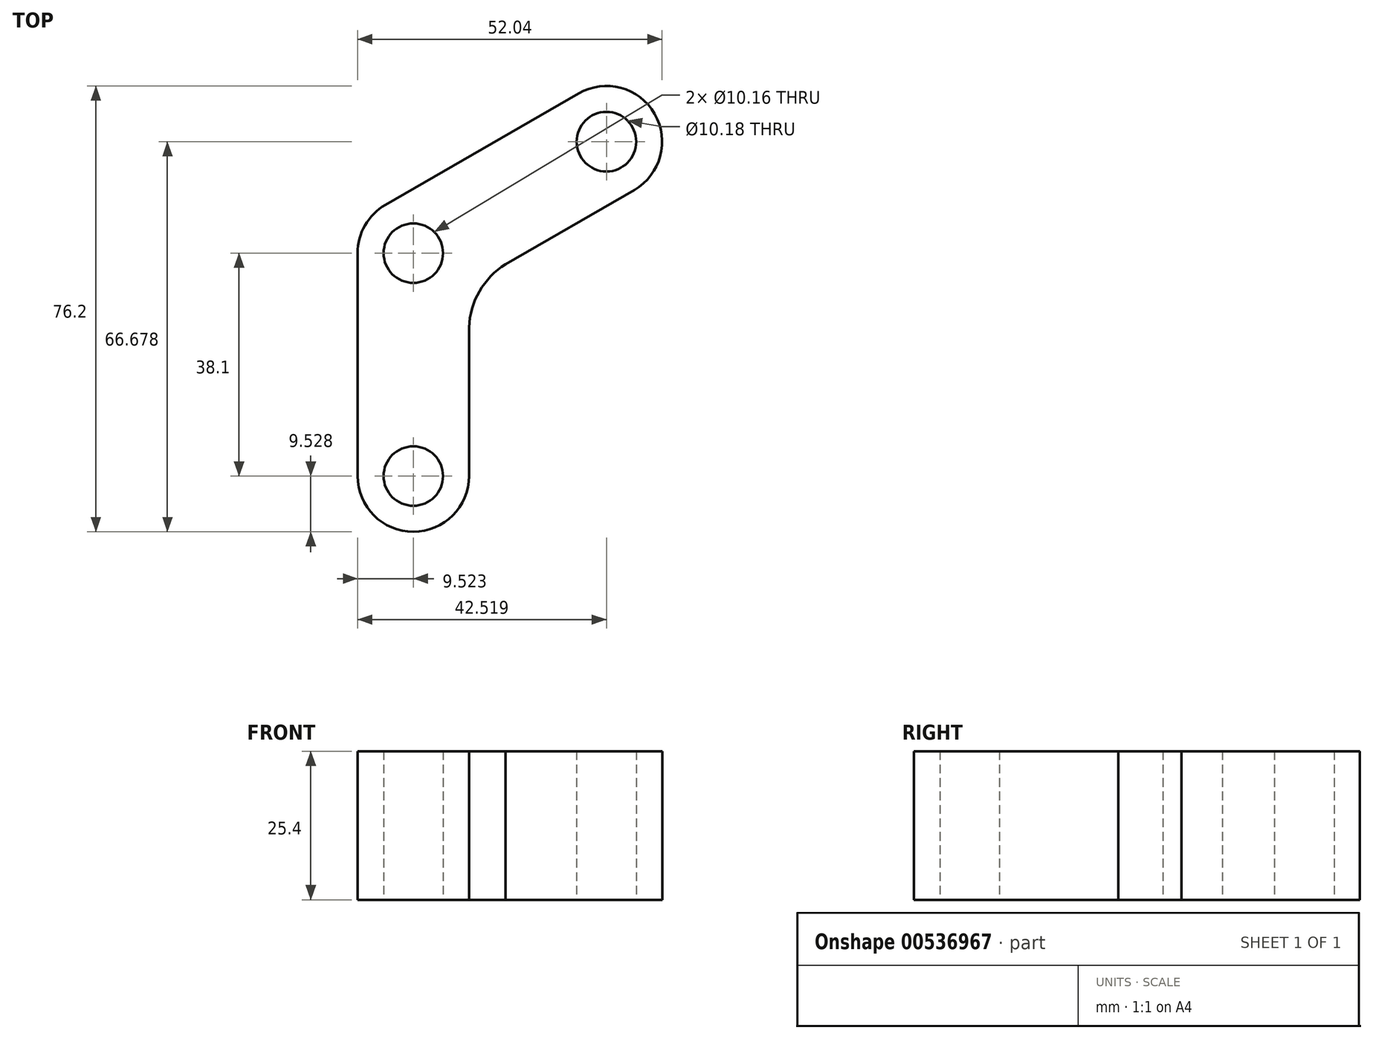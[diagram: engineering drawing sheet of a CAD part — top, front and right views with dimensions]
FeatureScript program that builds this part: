
annotation { "Feature Type Name" : "Feature", "Feature Type Description" : "" }
export const myFeature = defineFeature(function(context is Context, id is Id, definition is map)
    precondition{}
    {
        {
            var Q0;
            Q0=qCreatedBy(makeId("Top.planeOp"),FACE);
            var sketch = newSketch(context, id + "F0", { "sketchPlane" : qUnion([Q0])});
            skLineSegment(sketch, "E0.bottom", {"start": v(2.34, 0.08) * mm, "end": v(-16.71, 0.08) * mm});
            skLineSegment(sketch, "E0.top", {"start": v(2.34, 38.18) * mm, "end": v(-16.71, 38.18) * mm});
            skLineSegment(sketch, "E0.left", {"start": v(2.34, 0.08) * mm, "end": v(2.34, 38.18) * mm});
            skLineSegment(sketch, "E0.right", {"start": v(-16.71, 0.08) * mm, "end": v(-16.71, 38.18) * mm});
            skPoint(sketch, "E1", {"position": v(-7.19, 38.18) * mm});
            skLineSegment(sketch, "E2", {"start": v(-11.95, 46.43) * mm, "end": v(21.05, 65.48) * mm});
            skLineSegment(sketch, "E3", {"start": v(21.05, 65.48) * mm, "end": v(30.57, 48.98) * mm});
            skLineSegment(sketch, "E4", {"start": v(-7.19, 38.18) * mm, "end": v(25.8, 57.23) * mm, "construction": true});
            skLineSegment(sketch, "E5", {"start": v(-7.19, 38.18) * mm, "end": v(-7.19, 0.08) * mm, "construction": true});
            skPoint(sketch, "E6", {"position": v(25.8, 57.23) * mm});
            skLineSegment(sketch, "E7", {"start": v(-11.95, 46.43) * mm, "end": v(-2.42, 29.93) * mm});
            skLineSegment(sketch, "E8", {"start": v(30.57, 48.98) * mm, "end": v(-2.42, 29.93) * mm});
            skCircle(sketch, "E9", {"center": v(-7.19, 0.08) * mm, "radius": 9.53 * mm});
            skCircle(sketch, "E10", {"center": v(25.8, 57.23) * mm, "radius": 9.53 * mm});
            skCircle(sketch, "E11", {"center": v(-7.19, 38.18) * mm, "radius": 9.52 * mm});
            skLineSegment(sketch, "E12", {"start": v(-7.19, 0.08) * mm, "end": v(-2.1, 0.08) * mm});
            skLineSegment(sketch, "E13", {"start": v(-2.1, 0.08) * mm, "end": v(-7.19, 0.08) * mm});
            skLineSegment(sketch, "E14", {"start": v(-7.19, 38.18) * mm, "end": v(-9.73, 42.58) * mm});
            skLineSegment(sketch, "E15", {"start": v(-9.73, 42.58) * mm, "end": v(-7.19, 38.18) * mm});
            skLineSegment(sketch, "E16", {"start": v(25.8, 57.23) * mm, "end": v(28.35, 52.82) * mm});
            skLineSegment(sketch, "E17", {"start": v(28.35, 52.82) * mm, "end": v(25.8, 57.23) * mm});
            skCircle(sketch, "E18", {"center": v(25.8, 57.23) * mm, "radius": 5.1 * mm});
            skCircle(sketch, "E19", {"center": v(-7.19, 38.18) * mm, "radius": 5.08 * mm});
            skCircle(sketch, "E20", {"center": v(-7.19, 0.08) * mm, "radius": 5.08 * mm});
            skArc(sketch, "E21", {"start": v(9.32, 36.71) * mm, "mid": v(4.1, 31.66) * mm, "end": v(2.34, 24.61) * mm});
            skSolve(sketch);
        }
        {
            var Q0;
            Q0 = qSketchRegion(id + "F0", true);
            extrude(context, id + "F1", {"entities" : qUnion([Q0]), "endBound" : BoundingType.SYMMETRIC, "depth" : 25.4 * mm, "offsetDistance" : 25.4 * mm});
        }
        {
            var Q0;
            {var subQ1=sQuery(id+"F0.wireOp",EDGE,"E0.top");var subQ3=sQuery(id+"F0.wireOp",EDGE,"E19");var subQ4=makeQuery(id+"F0.imprint","INTERSECT",VERTEX,{"disambiguationData":[OD(0.0)],"derivedFrom":[subQ1,subQ3]});Q0=makeQuery(id+"F0.imprint","IMPRINT",FACE,{"disambiguationData":[TD([[makeQuery(id+"F0.imprint","IMPRINT",EDGE,{"disambiguationData":[TD([[subQ4,1.0]])],"derivedFrom":subQ3}),-1.0]])]});}
            extrude(context, id + "F2", {"entities" : qUnion([Q0]), "operationType" : NewBodyOperationType.ADD, "endBound" : BoundingType.SYMMETRIC, "depth" : 25.4 * mm, "offsetDistance" : 25.4 * mm});
        }
        {
            var Q0;
            {var subQ1=sQuery(id+"F0.wireOp",EDGE,"E0.left");var subQ3=sQuery(id+"F0.wireOp",EDGE,"E8");var subQ4=makeQuery(id+"F0.imprint","INTERSECT",VERTEX,{"derivedFrom":[subQ1,subQ3]});Q0=makeQuery(id+"F0.imprint","IMPRINT",FACE,{"disambiguationData":[TD([[makeQuery(id+"F0.imprint","IMPRINT",EDGE,{"disambiguationData":[TD([[subQ4,-1.0]])],"derivedFrom":subQ1}),1.0]])]});}
            extrude(context, id + "F3", {"entities" : qUnion([Q0]), "operationType" : NewBodyOperationType.ADD, "endBound" : BoundingType.SYMMETRIC, "depth" : 25.4 * mm, "offsetDistance" : 25.4 * mm});
        }
    });
